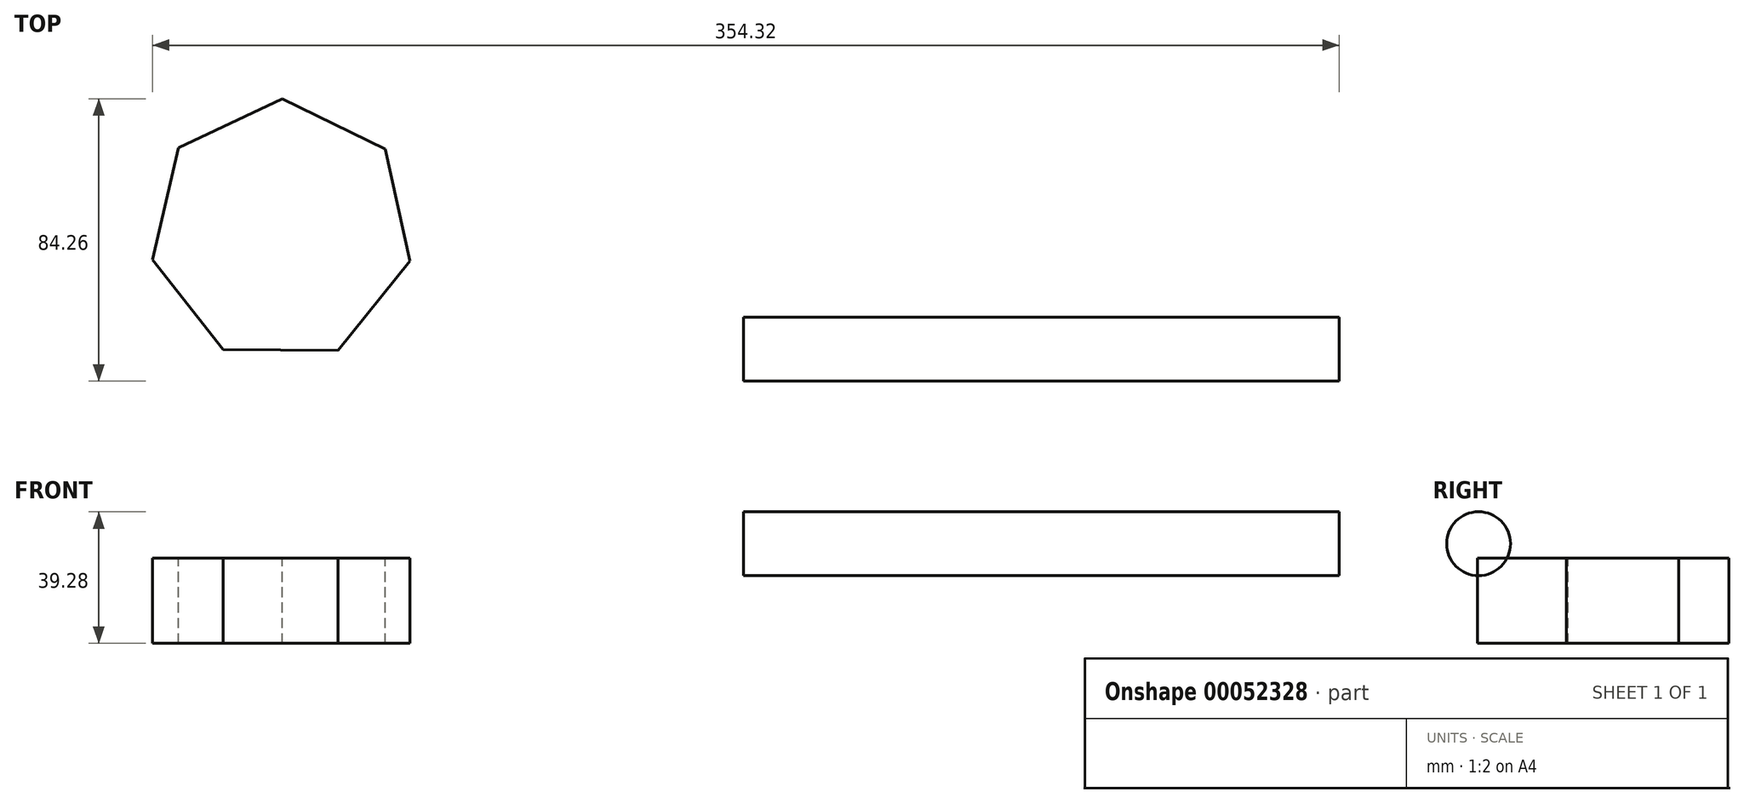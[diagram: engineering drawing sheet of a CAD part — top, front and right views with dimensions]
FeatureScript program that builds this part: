
annotation { "Feature Type Name" : "Feature", "Feature Type Description" : "" }
export const myFeature = defineFeature(function(context is Context, id is Id, definition is map)
    precondition{}
    {
        {
            var Q0;
            Q0=qCreatedBy(makeId("Right.planeOp"),FACE);
            var sketch = newSketch(context, id + "F0", { "sketchPlane" : qUnion([Q0])});
            skCircle(sketch, "E0", {"center": v(-45.4, 29.76) * mm, "radius": 9.53 * mm});
            skSolve(sketch);
        }
        {
            var Q0;
            Q0=sQuery(id+"F0.wireOp",EDGE,"E0");
            extrude(context, id + "F1", {"bodyType" : ToolBodyType.SURFACE, "surfaceEntities" : qUnion([Q0]), "depth" : 177.8 * mm});
        }
        {
            var Q0;
            Q0=qCreatedBy(makeId("Top.planeOp"),FACE);
            var sketch = newSketch(context, id + "F2", { "sketchPlane" : qUnion([Q0])});
            skCircle(sketch, "E1.cCircle", {"center": v(-138, -10.11) * mm, "radius": 35.55 * mm, "construction": true});
            skLineSegment(sketch, "E1.0", {"start": v(-137.77, 29.34) * mm, "end": v(-107.01, 14.3) * mm});
            skLineSegment(sketch, "E1.1", {"start": v(-107.01, 14.3) * mm, "end": v(-99.6, -19.12) * mm});
            skLineSegment(sketch, "E1.2", {"start": v(-99.6, -19.12) * mm, "end": v(-121.1, -45.76) * mm});
            skLineSegment(sketch, "E1.3", {"start": v(-121.1, -45.76) * mm, "end": v(-155.33, -45.56) * mm});
            skLineSegment(sketch, "E1.4", {"start": v(-155.33, -45.56) * mm, "end": v(-176.52, -18.67) * mm});
            skLineSegment(sketch, "E1.5", {"start": v(-176.52, -18.67) * mm, "end": v(-168.7, 14.67) * mm});
            skLineSegment(sketch, "E1.6", {"start": v(-168.7, 14.67) * mm, "end": v(-137.77, 29.34) * mm});
            skPoint(sketch, "E1.0.midPoint", {"position": v(-122.4, 21.82) * mm});
            skSolve(sketch);
        }
        {
            var Q0;
            Q0=makeQuery(id+"F2.imprint","IMPRINT",FACE,{"disambiguationData":[TD([[makeQuery(id+"F2.imprint","IMPRINT",EDGE,{"derivedFrom":sQuery(id+"F2.wireOp",EDGE,"E1.0")}),-1.0]])]});
            var Q1;
            Q1=sQuery(id+"F2.wireOp",EDGE,"E1.5");
            var Q2;
            Q2=sQuery(id+"F2.wireOp",EDGE,"E1.6");
            var Q3;
            Q3=sQuery(id+"F2.wireOp",EDGE,"E1.0");
            var Q4;
            Q4=sQuery(id+"F2.wireOp",EDGE,"E1.1");
            var Q5;
            Q5=sQuery(id+"F2.wireOp",EDGE,"E1.2");
            var Q6;
            Q6=sQuery(id+"F2.wireOp",EDGE,"E1.4");
            var Q7;
            Q7=sQuery(id+"F2.wireOp",EDGE,"E1.3");
            extrude(context, id + "F3", {"entities" : qUnion([Q0]), "bodyType" : ToolBodyType.SURFACE, "surfaceEntities" : qUnion([Q1, Q2, Q3, Q4, Q5, Q6, Q7]), "depth" : 25.4 * mm});
        }
    });
